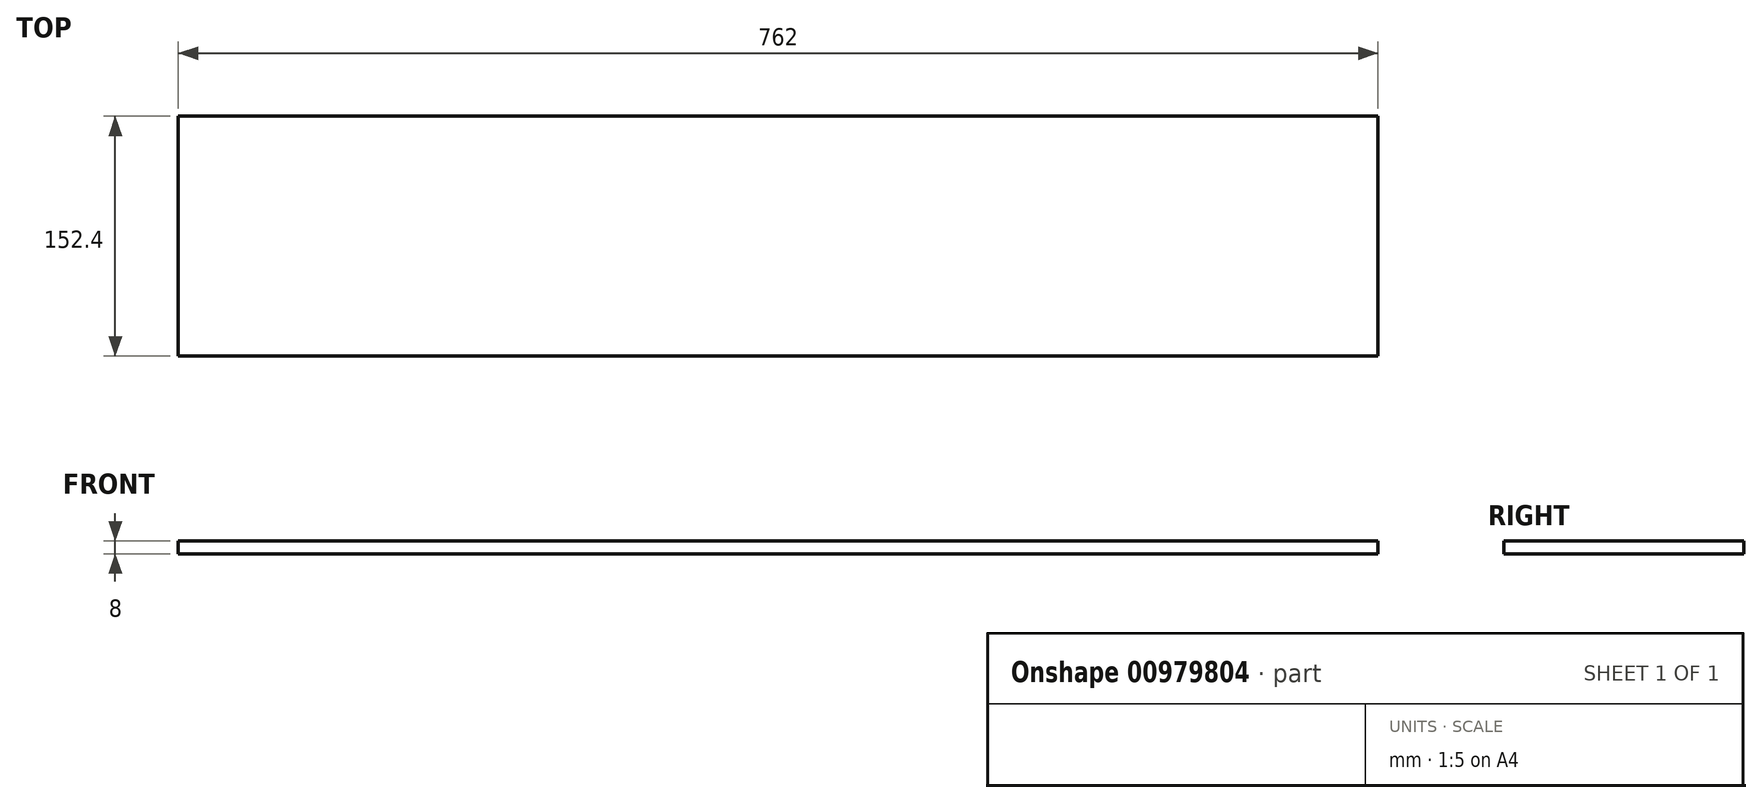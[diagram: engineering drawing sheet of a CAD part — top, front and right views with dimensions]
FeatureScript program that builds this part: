
annotation { "Feature Type Name" : "Feature", "Feature Type Description" : "" }
export const myFeature = defineFeature(function(context is Context, id is Id, definition is map)
    precondition{}
    {
        {
            var Q0;
            Q0=qCreatedBy(makeId("Top.planeOp"),FACE);
            var sketch = newSketch(context, id + "F0", { "sketchPlane" : qUnion([Q0])});
            skLineSegment(sketch, "E0.bottom", {"start": v(-586.26, 125.04) * mm, "end": v(175.74, 125.04) * mm});
            skLineSegment(sketch, "E0.top", {"start": v(-586.26, -27.36) * mm, "end": v(175.74, -27.36) * mm});
            skLineSegment(sketch, "E0.left", {"start": v(-586.26, 125.04) * mm, "end": v(-586.26, -27.36) * mm});
            skLineSegment(sketch, "E0.right", {"start": v(175.74, 125.04) * mm, "end": v(175.74, -27.36) * mm});
            skSolve(sketch);
        }
        {
            var Q0;
            Q0=qCreatedBy(makeId("Front.planeOp"),FACE);
            var sketch = newSketch(context, id + "F1", { "sketchPlane" : qUnion([Q0])});
            skSolve(sketch);
        }
        {
            var Q0;
            Q0 = qSketchRegion(id + "F1", true);
            var Q1;
            Q1=makeQuery(id+"F0.imprint","IMPRINT",FACE,{"disambiguationData":[TD([[makeQuery(id+"F0.imprint","IMPRINT",EDGE,{"derivedFrom":sQuery(id+"F0.wireOp",EDGE,"E0.bottom")}),-1.0]])]});
            extrude(context, id + "F2", {"entities" : qUnion([Q0, Q1]), "depth" : 8 * mm, "offsetDistance" : 25.4 * mm});
        }
    });
